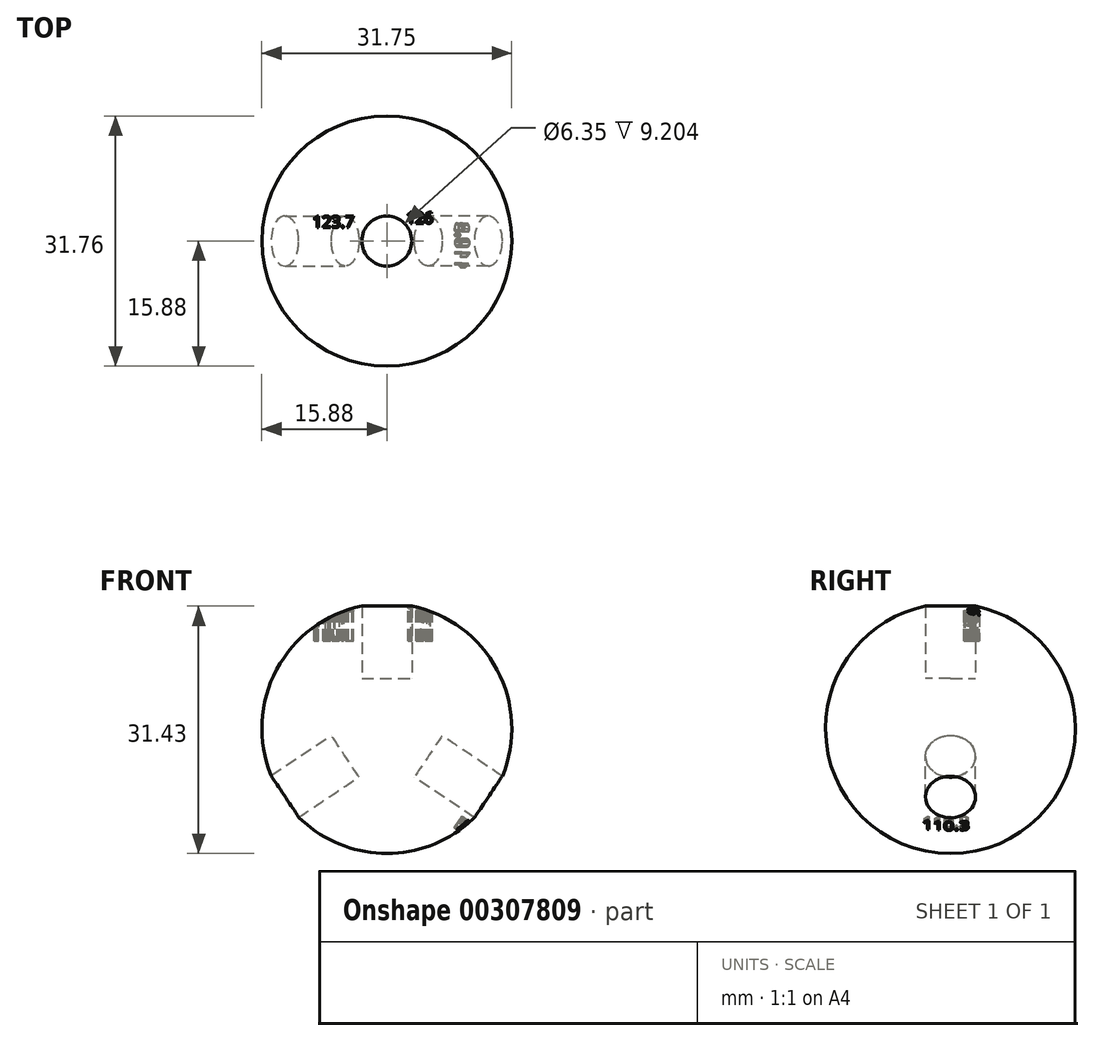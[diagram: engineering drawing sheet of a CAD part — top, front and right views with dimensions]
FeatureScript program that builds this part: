
annotation { "Feature Type Name" : "Feature", "Feature Type Description" : "" }
export const myFeature = defineFeature(function(context is Context, id is Id, definition is map)
    precondition{}
    {
        {
            var Q0;
            Q0=qCreatedBy(makeId("Top.planeOp"),FACE);
            var sketch = newSketch(context, id + "F0", { "sketchPlane" : qUnion([Q0])});
            skArc(sketch, "E0", {"start": v(0, 15.88) * mm, "mid": v(-15.88, 0) * mm, "end": v(0, -15.88) * mm});
            skLineSegment(sketch, "E1", {"start": v(0, 15.88) * mm, "end": v(0, -15.88) * mm});
            skSolve(sketch);
        }
        {
            var Q0;
            Q0=makeQuery(id+"F0.imprint","IMPRINT",FACE,{"disambiguationData":[TD([[makeQuery(id+"F0.imprint","IMPRINT",EDGE,{"derivedFrom":sQuery(id+"F0.wireOp",EDGE,"E0")}),1.0]])]});
            var Q1;
            Q1=sQuery(id+"F0.wireOp",EDGE,"E1");
            revolve(context, id + "F1", {"entities" : qUnion([Q0]), "axis" : qUnion([Q1]), "revolveType" : RevolveType.FULL});
        }
        {
            var Q0;
            Q0=qCreatedBy(makeId("Top.planeOp"),FACE);
            var sketch = newSketch(context, id + "F2", { "sketchPlane" : qUnion([Q0])});
            skLineSegment(sketch, "E2", {"start": v(0, 0) * mm, "end": v(0, 38.25) * mm, "construction": true});
            skLineSegment(sketch, "E3", {"start": v(0, 0) * mm, "end": v(64.34, 0) * mm, "construction": true});
            skSolve(sketch);
        }
        {
            var Q0;
            Q0=qCreatedBy(makeId("Top.planeOp"),FACE);
            cPlane(context, id + "F3", {"entities" : qUnion([Q0]), "cplaneType" : CPlaneType.OFFSET, "offset" : 6.35 * mm, "width" : 152.4 * mm, "height" : 152.4 * mm});
        }
        {
            var Q0;
            Q0=qCreatedBy(id+"F3.planeOp",FACE);
            var sketch = newSketch(context, id + "F4", { "sketchPlane" : qUnion([Q0])});
            skCircle(sketch, "E4", {"center": v(0, 0) * mm, "radius": 3.18 * mm});
            skSolve(sketch);
        }
        {
            var Q0;
            Q0 = qSketchRegion(id + "F4", true);
            extrude(context, id + "F5", {"entities" : qUnion([Q0]), "depth" : 25.4 * mm});
        }
        {
            var Q0;
            Q0=makeQuery(id+"F5.opExtrude","SWEPT_BODY",BODY,{"disambiguationData":[OSD([sQuery(id+"F4.wireOp",EDGE,"E4")])]});
            var Q1;
            Q1=sQuery(id+"F2.wireOp",EDGE,"E2");
            transform(context, id + "F6", {"entities" : qUnion([Q0]), "transformType" : TransformType.ROTATION, "transformAxis" : qUnion([Q1]), "angle" : 124 * degree, "makeCopy" : true});
        }
        {
            var Q0;
            Q0=makeQuery(id+"F6.opPattern","COPY",BODY,{"derivedFrom":makeQuery(id+"F5.opExtrude","SWEPT_BODY",BODY,{"disambiguationData":[OSD([sQuery(id+"F4.wireOp",EDGE,"E4")])]}),"instanceName":"1"});
            var Q1;
            Q1=sQuery(id+"F2.wireOp",EDGE,"E2");
            transform(context, id + "F7", {"entities" : qUnion([Q0]), "transformType" : TransformType.ROTATION, "transformAxis" : qUnion([Q1]), "angle" : 112.3 * degree, "makeCopy" : true});
        }
        {
            var Q0;
            Q0=makeQuery(id+"F5.opExtrude","CAP_FACE",FACE,{"disambiguationData":[OSD([sQuery(id+"F4.wireOp",EDGE,"E4")])],"isStart":false});
            cPlane(context, id + "F8", {"entities" : qUnion([Q0]), "cplaneType" : CPlaneType.OFFSET, "offset" : 14.25 * mm, "oppositeDirection" : true, "width" : 152.4 * mm, "height" : 152.4 * mm});
        }
        {
            var Q0;
            Q0=qCreatedBy(id+"F8.planeOp",FACE);
            var sketch = newSketch(context, id + "F9", { "sketchPlane" : qUnion([Q0])});
            skText(sketch, "E5", { "text": "123.7", "fontName": "OpenSans-Regular.ttf"});
            skText(sketch, "E6", { "text": "126", "fontName": "OpenSans-Regular.ttf"});
            const initialGuessF9  = {"E5": [-0.0094, 0.0017, 1, 0, 0.00148], "E6": [0.00249, 0.00224, 1, 0, 0.00142]};
            skSetInitialGuess(sketch, initialGuessF9);
            skSolve(sketch);
        }
        {
            var Q0;
            Q0 = qSketchRegion(id + "F9", true);
            extrude(context, id + "F10", {"entities" : qUnion([Q0]), "operationType" : NewBodyOperationType.REMOVE, "oppositeDirection" : true, "depth" : 6.35 * mm});
        }
        {
            var Q0;
            Q0=makeQuery(id+"F6.opPattern","COPY",FACE,{"derivedFrom":makeQuery(id+"F5.opExtrude","CAP_FACE",FACE,{"disambiguationData":[OSD([sQuery(id+"F4.wireOp",EDGE,"E4")])],"isStart":false}),"instanceName":"1"});
            cPlane(context, id + "F11", {"entities" : qUnion([Q0]), "cplaneType" : CPlaneType.OFFSET, "offset" : 13 * mm, "oppositeDirection" : true, "width" : 152.4 * mm, "height" : 152.4 * mm});
        }
        {
            var Q0;
            Q0=qCreatedBy(id+"F11.planeOp",FACE);
            var sketch = newSketch(context, id + "F12", { "sketchPlane" : qUnion([Q0])});
            skText(sketch, "E7", { "text": "110.3", "fontName": "OpenSans-Regular.ttf"});
            const initialGuessF12  = {"E7": [-0.0036, -0.0056, 1, 0, 0.0017]};
            skSetInitialGuess(sketch, initialGuessF12);
            skSolve(sketch);
        }
        {
            var Q0;
            Q0 = qSketchRegion(id + "F12", true);
            extrude(context, id + "F13", {"entities" : qUnion([Q0]), "operationType" : NewBodyOperationType.REMOVE, "oppositeDirection" : true, "depth" : 4.57 * mm});
        }
        {
            var Q0;
            Q0=makeQuery(id+"F5.opExtrude","SWEPT_BODY",BODY,{"disambiguationData":[OSD([sQuery(id+"F4.wireOp",EDGE,"E4")])]});
            var Q1;
            Q1=makeQuery(id+"F7.opPattern","COPY",BODY,{"derivedFrom":makeQuery(id+"F6.opPattern","COPY",BODY,{"derivedFrom":makeQuery(id+"F5.opExtrude","SWEPT_BODY",BODY,{"disambiguationData":[OSD([sQuery(id+"F4.wireOp",EDGE,"E4")])]}),"instanceName":"1"}),"instanceName":"1"});
            var Q2;
            Q2=makeQuery(id+"F6.opPattern","COPY",BODY,{"derivedFrom":makeQuery(id+"F5.opExtrude","SWEPT_BODY",BODY,{"disambiguationData":[OSD([sQuery(id+"F4.wireOp",EDGE,"E4")])]}),"instanceName":"1"});
            var Q3;
            Q3=makeQuery(id+"F1.opRevolve","SWEPT_BODY",BODY,{"disambiguationData":[OSD([sQuery(id+"F0.wireOp",EDGE,"E0"),sQuery(id+"F0.wireOp",EDGE,"E1")])]});
            booleanBodies(context, id + "F14", {"operationType" : BooleanOperationType.SUBTRACTION, "tools" : qUnion([Q0, Q1, Q2]), "targets" : qUnion([Q3])});
        }
    });
